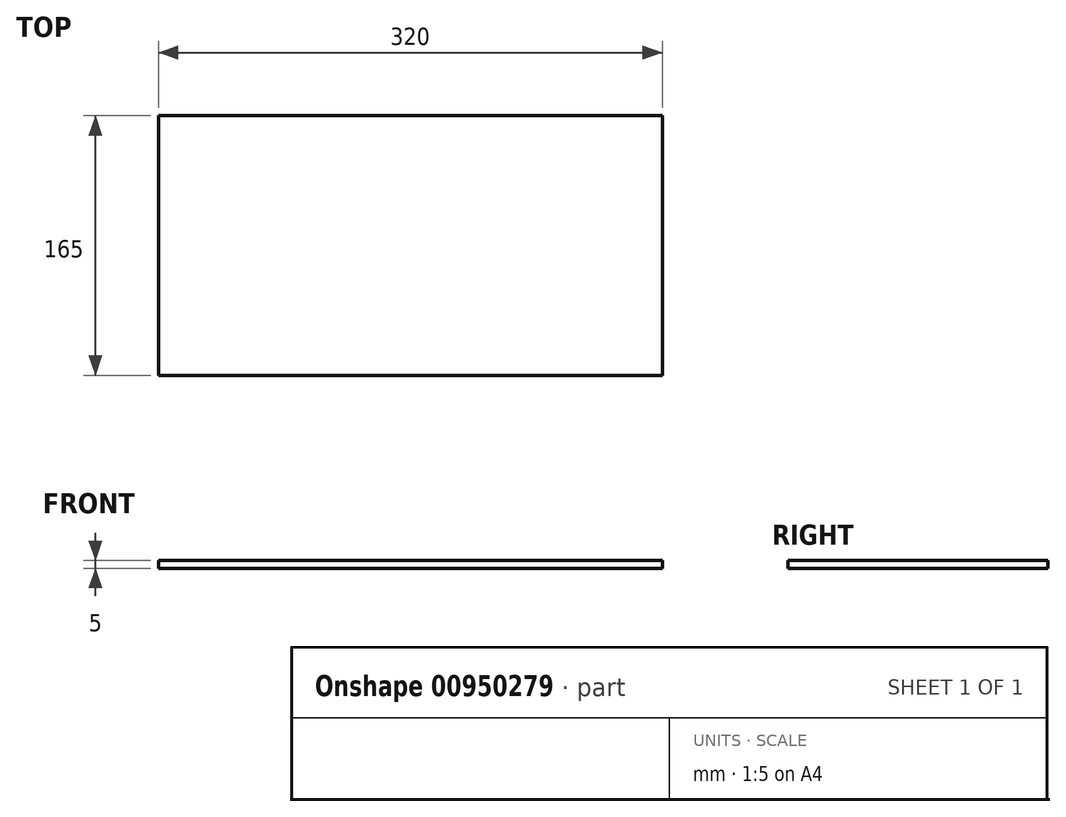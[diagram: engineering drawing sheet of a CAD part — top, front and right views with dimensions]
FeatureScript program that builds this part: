
annotation { "Feature Type Name" : "Feature", "Feature Type Description" : "" }
export const myFeature = defineFeature(function(context is Context, id is Id, definition is map)
    precondition{}
    {
        {
            var Q0;
            Q0=qCreatedBy(makeId("Top.planeOp"),FACE);
            var sketch = newSketch(context, id + "F0", { "sketchPlane" : qUnion([Q0])});
            skLineSegment(sketch, "E0.bottom", {"start": v(160, -82.5) * mm, "end": v(-160, -82.5) * mm});
            skLineSegment(sketch, "E0.top", {"start": v(160, 82.5) * mm, "end": v(-160, 82.5) * mm});
            skLineSegment(sketch, "E0.left", {"start": v(160, -82.5) * mm, "end": v(160, 82.5) * mm});
            skLineSegment(sketch, "E0.right", {"start": v(-160, -82.5) * mm, "end": v(-160, 82.5) * mm});
            skPoint(sketch, "E0.middle", {"position": v(0, 0) * mm});
            skSolve(sketch);
        }
        {
            var Q0;
            Q0=makeQuery(id+"F0.imprint","IMPRINT",FACE,{"disambiguationData":[TD([[makeQuery(id+"F0.imprint","IMPRINT",EDGE,{"derivedFrom":sQuery(id+"F0.wireOp",EDGE,"E0.bottom")}),-1.0]])]});
            extrude(context, id + "F1", {"entities" : qUnion([Q0]), "endBound" : BoundingType.SYMMETRIC, "depth" : 5 * mm, "offsetDistance" : 25 * mm});
        }
    });
